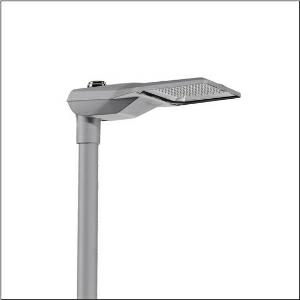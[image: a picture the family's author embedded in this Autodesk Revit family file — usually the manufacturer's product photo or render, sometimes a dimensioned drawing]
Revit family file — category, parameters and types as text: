
# Revit family: streetlight_sl_21_midi___st1_0a_5xe7d37n08nb_cbe6
name_source: partatom
category: Lighting Fixtures
units: mm (PartAtom-declared; Revit-internal decimal feet)

## family parameters
Cut with Voids When Loaded = No
Host = Face
Light Source = No
Part Type = Normal
Room Calculation Point = No
Round Connector Dimension = Use Diameter
Shared = No

## types (1)
- --- (1 x LED, 22700 lm, 151.2 W, 3000K)
    Apparent Load = 151 VA
    CIE Flux Codes = 40 73 97 100 100
    Color Rendering = 70
    Color Temperature = 3000K
    Default Elevation = 1800 mm
    Description = Streetlight SL 21 midi, mast luminaire, primary light control with lens, of PMMA, primary optical cover: cover, of toughened safety glass, transparent, light distribution: ST1.0a, light emission: direct distribution, primary light characteristic: asymmetric, installation type: side-entry, LED, 3G 2.5mm², High Power LED, rated luminous flux: 22.700lm, luminous efficacy: 150lm/W, light colour: 730, colour temperature: 3000K, control gear: NEMA (7pin), control: overheat protection, pre-setting: linear dimming characteristic, constant luminous flux control, time-dependent luminous flux control, flexible luminous flux parameterisation, mains connection: 220..240V, AC, 50/60Hz, connection cable pre-assembled, cable length: 12,5m, wiring characteristics: H05VV-F, start of lifetime: 151W, end of service life: 157W, reduction: 70W, luminaire housing, of diecast aluminium (EN AC-44300), powder-coated, SITECO metallic grey (DB 702S), corrosivity category C5 high according to DIN EN ISO 12944, multi-level sealing system, sealing non-destructively replaceable, inclination adjustable: 0°, 5°, 10°, 15°, length: 644mm, width: 335mm, height: 110mm, spigot size: 42mm (side-entry), mounting height: 4..8m, protection rating (complete): IP66, insulation class (complete): insulation class I (protective earthing), certification: CE, ENEC, ENEC+, VDE, impact resistance: IK10, permissible operating ambient temperature for outdoor applications: -40..+50°C, standard-compliant lighting for roads and squares, packaging unit: 1 piece

Light Distribution: ST1.0a
    Height = 111 mm
    Lamp = 1 x LED
    Lamp Light Flux = 22700 lm
    Lamp Power = 151.2 W
    Lamp count = 1
    Length = 644 mm
    Luminous efficacy = 150 lm/W
    Manufacturer = Siteco
    ModVariant = No
    Model = 5XE7D37N08NB
    Number of Poles = 1
    OnlyDefault = Yes
    Power Factor = 1
    Product Name = Streetlight SL 21 midi | ST1.0a
    Product group = mast luminaire | pylon top
    ProductGroupID = 6100
    Protection Class = Protection class I
    Protection Degree = IP 66
    RLX_Detail_Level = 1
    RLX_Emergency_Light_Flux = 0 lm
    RLX_Emergency_Type = 0
    RLX_Emergency_Type_DB = No
    RlxData = <blob elided: 26605 chars, md5=9d735ebd>
    Socket = socket
    Standby Power = 0 W
    System Light Flux = 22700 lm
    System Power = 151 W
    Type Comments = factory setting: luminous flux: 100 % | dim-lin: 254 | 802 mA
    Type Image = l_1294377.jpg
    URL = http://relux.com
    VarID = @adj_134661
    Voltage = 0 V
    Weight = 0.00 kg
    Width = 336 mm

## geometry (parser evidence)
native form markers: Blend x4, Sweep x11
no freeform markers — native parametric forms only
